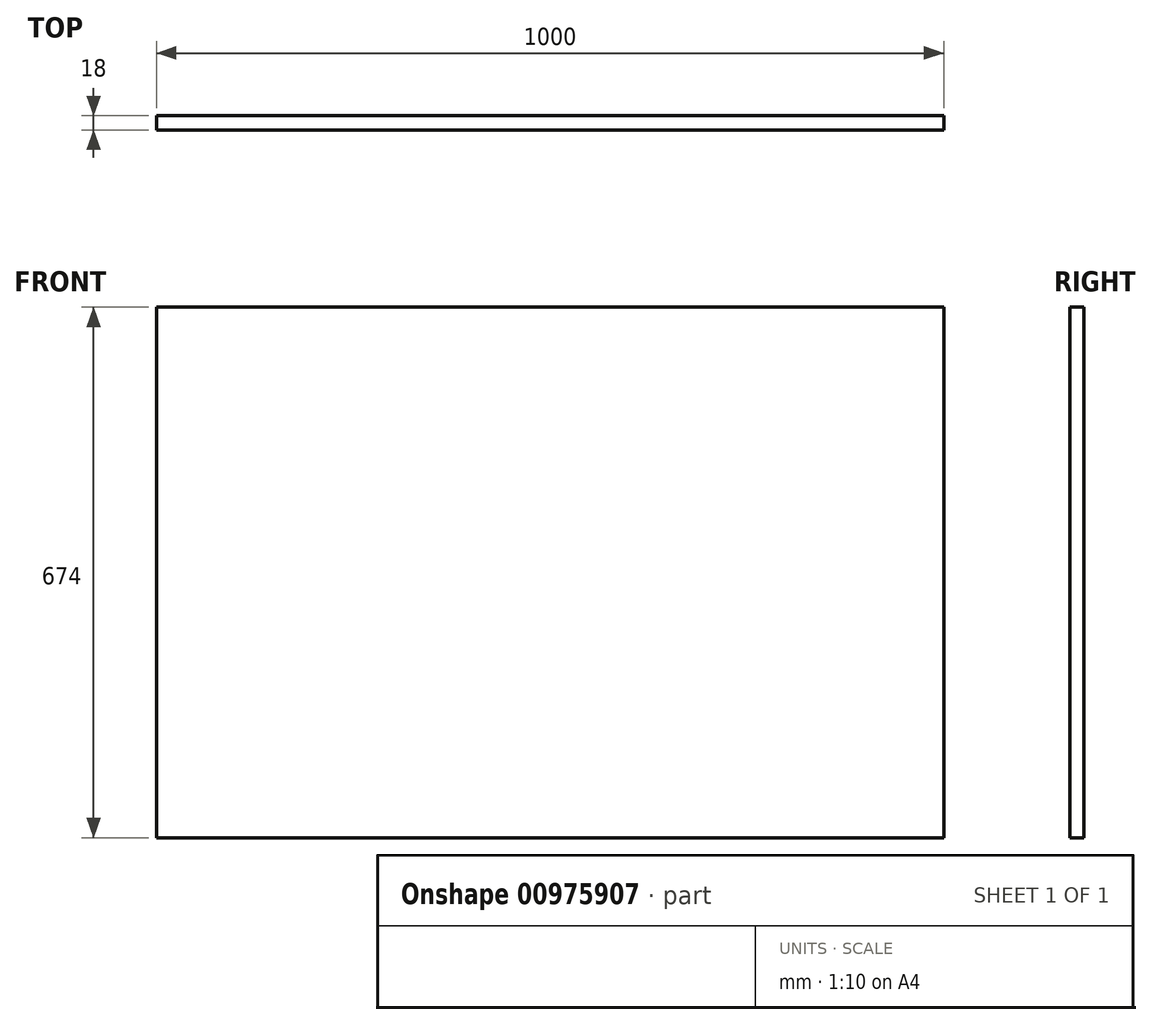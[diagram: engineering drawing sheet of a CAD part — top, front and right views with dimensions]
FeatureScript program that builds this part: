
annotation { "Feature Type Name" : "Feature", "Feature Type Description" : "" }
export const myFeature = defineFeature(function(context is Context, id is Id, definition is map)
    precondition{}
    {
        {
            var Q0;
            Q0=qCreatedBy(makeId("Front.planeOp"),FACE);
            var sketch = newSketch(context, id + "F0", { "sketchPlane" : qUnion([Q0])});
            skLineSegment(sketch, "E0.bottom", {"start": v(-831.6, 641.8) * mm, "end": v(168.4, 641.8) * mm});
            skLineSegment(sketch, "E0.top", {"start": v(-831.6, -32.2) * mm, "end": v(168.4, -32.2) * mm});
            skLineSegment(sketch, "E0.left", {"start": v(-831.6, 641.8) * mm, "end": v(-831.6, -32.2) * mm});
            skLineSegment(sketch, "E0.right", {"start": v(168.4, 641.8) * mm, "end": v(168.4, -32.2) * mm});
            skSolve(sketch);
        }
        {
            var Q0;
            Q0=makeQuery(id+"F0.imprint","IMPRINT",FACE,{"disambiguationData":[TD([[makeQuery(id+"F0.imprint","IMPRINT",EDGE,{"derivedFrom":sQuery(id+"F0.wireOp",EDGE,"E0.bottom")}),-1.0]])]});
            extrude(context, id + "F1", {"entities" : qUnion([Q0]), "depth" : 18 * mm, "offsetDistance" : 25 * mm});
        }
    });
